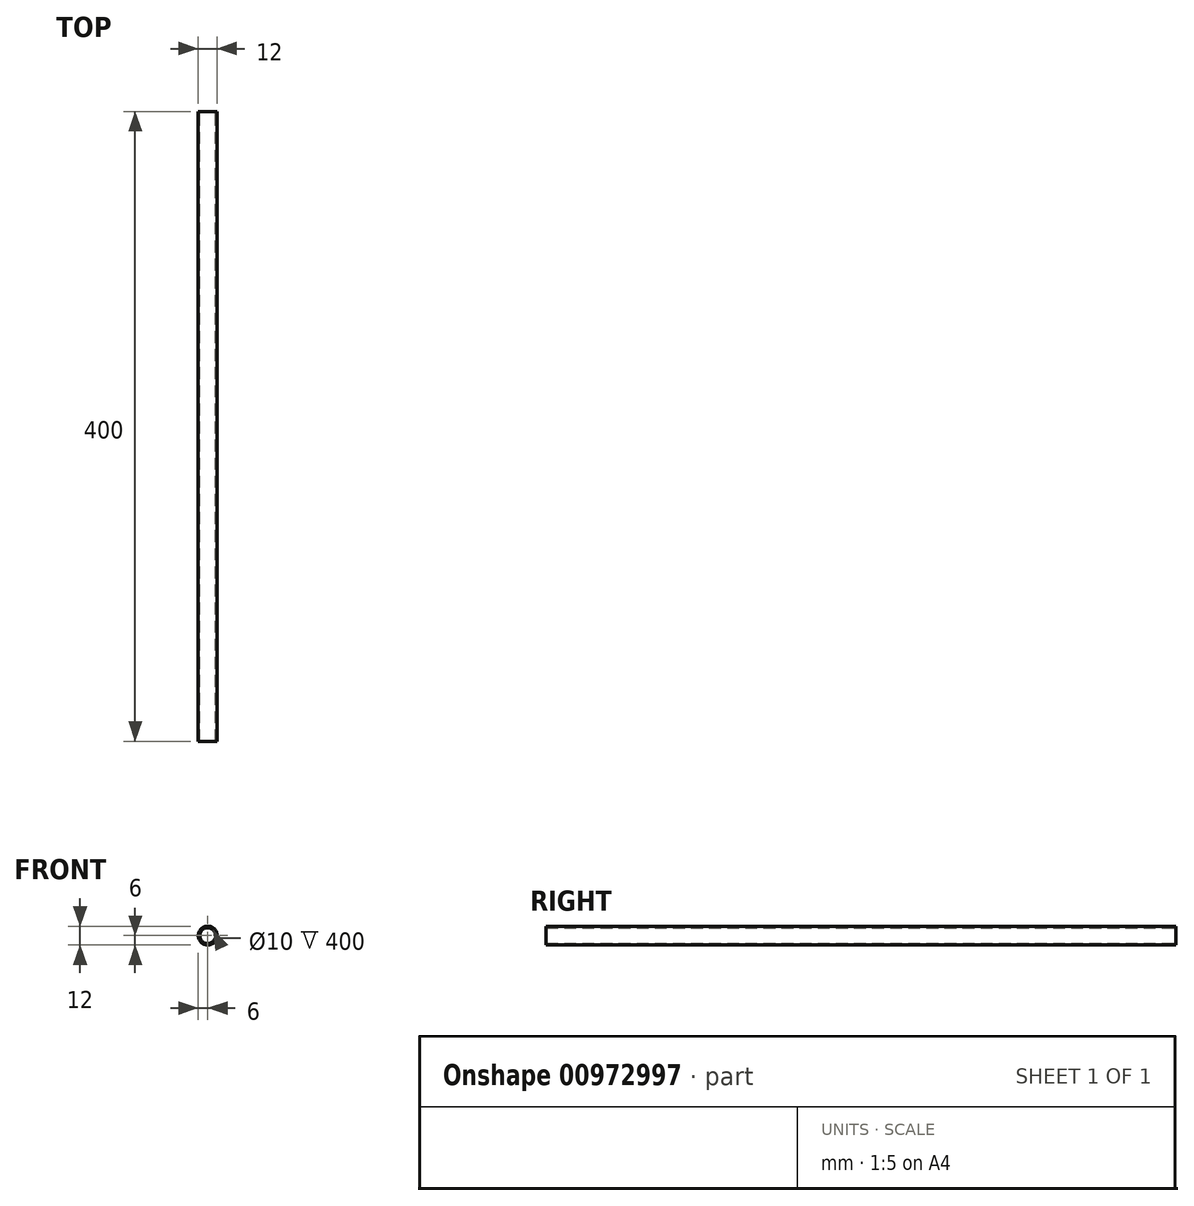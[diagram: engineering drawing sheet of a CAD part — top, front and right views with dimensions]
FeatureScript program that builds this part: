
annotation { "Feature Type Name" : "Feature", "Feature Type Description" : "" }
export const myFeature = defineFeature(function(context is Context, id is Id, definition is map)
    precondition{}
    {
        {
            var Q0;
            Q0=qCreatedBy(makeId("Front.planeOp"),FACE);
            var sketch = newSketch(context, id + "F0", { "sketchPlane" : qUnion([Q0])});
            skCircle(sketch, "E0", {"center": v(0, 0) * mm, "radius": 6 * mm});
            skCircle(sketch, "E1", {"center": v(0, 0) * mm, "radius": 5 * mm});
            skSolve(sketch);
        }
        {
            var Q0;
            Q0=makeQuery(id+"F0.imprint","IMPRINT",FACE,{"disambiguationData":[TD([[makeQuery(id+"F0.imprint","IMPRINT",EDGE,{"derivedFrom":sQuery(id+"F0.wireOp",EDGE,"E0")}),1.0]])]});
            extrude(context, id + "F1", {"entities" : qUnion([Q0]), "depth" : 400 * mm, "offsetDistance" : 25 * mm});
        }
    });
